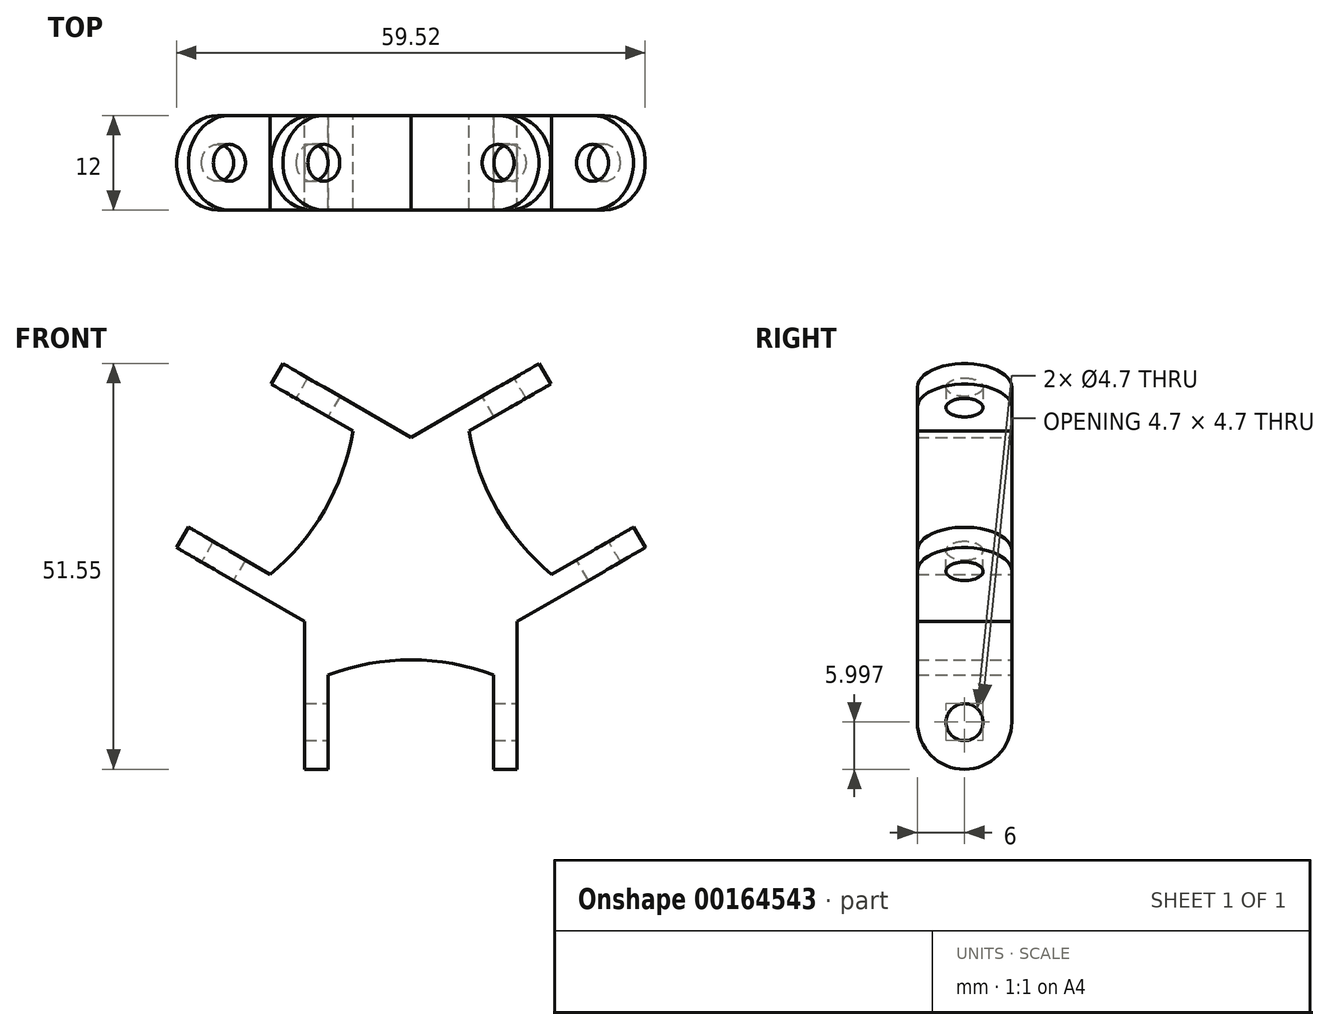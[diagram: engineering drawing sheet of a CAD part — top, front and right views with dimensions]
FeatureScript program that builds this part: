
annotation { "Feature Type Name" : "Feature", "Feature Type Description" : "" }
export const myFeature = defineFeature(function(context is Context, id is Id, definition is map)
    precondition{}
    {
        {
            var Q0;
            Q0=qCreatedBy(makeId("Front.planeOp"),FACE);
            var sketch = newSketch(context, id + "F0", { "sketchPlane" : qUnion([Q0])});
            skCircle(sketch, "E0", {"center": v(0, 0) * mm, "radius": 30 * mm, "construction": true});
            skLineSegment(sketch, "E1", {"start": v(0, 0) * mm, "end": v(0, 27.8) * mm, "construction": true});
            skLineSegment(sketch, "E2", {"start": v(0, 0) * mm, "end": v(24.85, -14.35) * mm, "construction": true});
            skLineSegment(sketch, "E3", {"start": v(38.06, 38.48) * mm, "end": v(52.36, 13.72) * mm, "construction": true});
            skLineSegment(sketch, "E4", {"start": v(0, 0) * mm, "end": v(45.2, 26.1) * mm, "construction": true});
            skLineSegment(sketch, "E5", {"start": v(17.76, 22.38) * mm, "end": v(8.6, 17.09) * mm});
            skLineSegment(sketch, "E6", {"start": v(28.26, 4.2) * mm, "end": v(19.1, -1.1) * mm});
            skArc(sketch, "E7", {"start": v(8.6, 17.09) * mm, "mid": v(12.2, 7.05) * mm, "end": v(19.1, -1.1) * mm, "construction": true});
            skLineSegment(sketch, "E8", {"start": v(19.09, 23.14) * mm, "end": v(24.34, 14.05) * mm, "construction": true});
            skLineSegment(sketch, "E9", {"start": v(24.34, 14.05) * mm, "end": v(29.59, 4.96) * mm, "construction": true});
            skLineSegment(sketch, "E10", {"start": v(13.84, 20.12) * mm, "end": v(24.34, 1.93) * mm, "construction": true});
            skLineSegment(sketch, "E11", {"start": v(13.5, -7.8) * mm, "end": v(21.63, -3.1) * mm, "construction": true});
            skLineSegment(sketch, "E12.MirrorCS", {"start": v(0, 15.59) * mm, "end": v(8.13, 20.28) * mm, "construction": true});
            skPoint(sketch, "E13.center", {"position": v(0.48, 0.8) * mm});
            skLineSegment(sketch, "E13.anchor1", {"start": v(0.48, 0.8) * mm, "end": v(0, 0) * mm, "construction": true});
            skLineSegment(sketch, "E13.anchor2", {"start": v(0.48, 0.8) * mm, "end": v(1.42, 0.8) * mm, "construction": true});
            skLineSegment(sketch, "E14", {"start": v(17.76, 22.38) * mm, "end": v(16.26, 24.98) * mm});
            skLineSegment(sketch, "E15", {"start": v(16.26, 24.98) * mm, "end": v(0, 15.59) * mm});
            skLineSegment(sketch, "E16", {"start": v(8.6, 17.09) * mm, "end": v(7.37, 16.38) * mm});
            skLineSegment(sketch, "E17", {"start": v(19.1, -1.1) * mm, "end": v(17.87, -1.8) * mm});
            skLineSegment(sketch, "E18", {"start": v(28.26, 4.2) * mm, "end": v(29.76, 1.6) * mm});
            skLineSegment(sketch, "E19", {"start": v(29.76, 1.6) * mm, "end": v(13.5, -7.8) * mm});
            skArc(sketch, "E20", {"start": v(7.37, 16.38) * mm, "mid": v(10.98, 6.34) * mm, "end": v(17.87, -1.8) * mm});
            skLineSegment(sketch, "E21.1.0", {"start": v(-29.76, 1.6) * mm, "end": v(-13.5, -7.8) * mm});
            skLineSegment(sketch, "E21.1.1", {"start": v(-28.26, 4.2) * mm, "end": v(-29.76, 1.6) * mm});
            skLineSegment(sketch, "E21.1.2", {"start": v(-28.26, 4.2) * mm, "end": v(-19.1, -1.1) * mm});
            skLineSegment(sketch, "E21.1.3", {"start": v(-19.1, -1.1) * mm, "end": v(-17.87, -1.8) * mm});
            skArc(sketch, "E21.1.4", {"start": v(-17.87, -1.8) * mm, "mid": v(-10.98, 6.34) * mm, "end": v(-7.37, 16.38) * mm});
            skLineSegment(sketch, "E21.1.5", {"start": v(-8.6, 17.09) * mm, "end": v(-7.37, 16.38) * mm});
            skLineSegment(sketch, "E21.1.6", {"start": v(-17.76, 22.38) * mm, "end": v(-8.6, 17.09) * mm});
            skLineSegment(sketch, "E21.1.7", {"start": v(-17.76, 22.38) * mm, "end": v(-16.26, 24.98) * mm});
            skLineSegment(sketch, "E21.1.8", {"start": v(-16.26, 24.98) * mm, "end": v(0, 15.59) * mm});
            skLineSegment(sketch, "E21.2.0", {"start": v(13.5, -26.57) * mm, "end": v(13.5, -7.8) * mm});
            skLineSegment(sketch, "E21.2.1", {"start": v(10.5, -26.57) * mm, "end": v(13.5, -26.57) * mm});
            skLineSegment(sketch, "E21.2.2", {"start": v(10.5, -26.57) * mm, "end": v(10.5, -16) * mm});
            skLineSegment(sketch, "E21.2.3", {"start": v(10.5, -16) * mm, "end": v(10.5, -14.57) * mm});
            skArc(sketch, "E21.2.4", {"start": v(10.5, -14.57) * mm, "mid": v(0, -12.68) * mm, "end": v(-10.5, -14.57) * mm});
            skLineSegment(sketch, "E21.2.5", {"start": v(-10.5, -16) * mm, "end": v(-10.5, -14.57) * mm});
            skLineSegment(sketch, "E21.2.6", {"start": v(-10.5, -26.57) * mm, "end": v(-10.5, -16) * mm});
            skLineSegment(sketch, "E21.2.7", {"start": v(-10.5, -26.57) * mm, "end": v(-13.5, -26.57) * mm});
            skLineSegment(sketch, "E21.2.8", {"start": v(-13.5, -26.57) * mm, "end": v(-13.5, -7.8) * mm});
            skSolve(sketch);
        }
        {
            var Q0;
            Q0=qCreatedBy(makeId("Front.planeOp"),FACE);
            var sketch = newSketch(context, id + "F1", { "sketchPlane" : qUnion([Q0])});
            skLineSegment(sketch, "E22.0", {"start": v(13.84, 20.12) * mm, "end": v(24.34, 1.93) * mm, "construction": true});
            skLineSegment(sketch, "E23.0", {"start": v(19.76, -0.14) * mm, "end": v(17.26, 4.2) * mm});
            skArc(sketch, "E23.1", {"start": v(8.7, 16.57) * mm, "mid": v(12.2, 7.05) * mm, "end": v(18.7, -0.75) * mm});
            skLineSegment(sketch, "E24.trimOffspring", {"start": v(9.76, 17.18) * mm, "end": v(8.7, 16.57) * mm});
            skLineSegment(sketch, "E25.trimOffspring", {"start": v(19.76, -0.14) * mm, "end": v(18.7, -0.75) * mm});
            skLineSegment(sketch, "E26", {"start": v(12.26, 12.85) * mm, "end": v(13.13, 13.35) * mm});
            skLineSegment(sketch, "E27", {"start": v(13.13, 13.35) * mm, "end": v(18.13, 4.7) * mm});
            skLineSegment(sketch, "E28", {"start": v(18.13, 4.7) * mm, "end": v(17.26, 4.2) * mm});
            skLineSegment(sketch, "E29.trimOffspring", {"start": v(12.26, 12.85) * mm, "end": v(9.76, 17.18) * mm});
            skPoint(sketch, "E30.orphan", {"position": v(8.6, 17.09) * mm});
            skSolve(sketch);
        }
        {
            var Q0;
            Q0 = qSketchRegion(id + "F1", true);
            var Q1;
            Q1=sQuery(id+"F1.wireOp",EDGE,"E22.0");
            revolve(context, id + "F2", {"entities" : qUnion([Q0]), "axis" : qUnion([Q1]), "revolveType" : RevolveType.FULL});
        }
        {
            var Q0;
            Q0 = qSketchRegion(id + "F0", true);
            extrude(context, id + "F3", {"entities" : qUnion([Q0]), "endBound" : BoundingType.SYMMETRIC, "depth" : 12 * mm});
        }
        {
            var Q0;
            Q0=makeQuery(id+"F3.opExtrude","SWEPT_FACE",FACE,{"disambiguationData":[OSD([sQuery(id+"F0.wireOp",EDGE,"E15")])]});
            var sketch = newSketch(context, id + "F4", { "sketchPlane" : qUnion([Q0])});
            skArc(sketch, "E31", {"start": v(20.57, -6) * mm, "mid": v(26.57, 0) * mm, "end": v(20.57, 6) * mm});
            skLineSegment(sketch, "E32", {"start": v(20.57, 6) * mm, "end": v(20.57, 9.05) * mm});
            skLineSegment(sketch, "E33", {"start": v(20.57, 9.05) * mm, "end": v(30.54, 9.05) * mm});
            skLineSegment(sketch, "E34", {"start": v(30.54, 9.05) * mm, "end": v(30.54, -9.05) * mm});
            skLineSegment(sketch, "E35", {"start": v(30.54, -9.05) * mm, "end": v(20.57, -9.05) * mm});
            skLineSegment(sketch, "E36", {"start": v(20.57, -9.05) * mm, "end": v(20.57, -6) * mm});
            skCircle(sketch, "E37", {"center": v(20.57, 0) * mm, "radius": 2.35 * mm});
            skLineSegment(sketch, "E38", {"start": v(0, 19.84) * mm, "end": v(0, -19.76) * mm, "construction": true});
            skSolve(sketch);
        }
        {
            var Q0;
            Q0 = qSketchRegion(id + "F4", true);
            extrude(context, id + "F5", {"entities" : qUnion([Q0]), "oppositeDirection" : true, "depth" : 27 * mm});
        }
        {
            var Q0;
            Q0=makeQuery(id+"F5.opExtrude","SWEPT_BODY",BODY,{"disambiguationData":[OSD([sQuery(id+"F4.wireOp",EDGE,"E31"),sQuery(id+"F4.wireOp",EDGE,"E32"),sQuery(id+"F4.wireOp",EDGE,"E33"),sQuery(id+"F4.wireOp",EDGE,"E34"),sQuery(id+"F4.wireOp",EDGE,"E35"),sQuery(id+"F4.wireOp",EDGE,"E36")])]});
            var Q1;
            Q1=makeQuery(id+"F5.opExtrude","SWEPT_BODY",BODY,{"disambiguationData":[OSD([sQuery(id+"F4.wireOp",EDGE,"E37")])]});
            var Q2;
            Q2=sQuery(id+"F0.wireOp",EDGE,"E0");
            circularPattern(context, id + "F6", {"operationType" : NewBodyOperationType.REMOVE, "entities" : qUnion([Q0, Q1]), "axis" : qUnion([Q2]), "angle" : 120 * degree, "instanceCount" : 3});
        }
        {
            var Q0;
            Q0=makeQuery(id+"F2.opRevolve","SWEPT_BODY",BODY,{"disambiguationData":[OSD([sQuery(id+"F1.wireOp",EDGE,"E23.0"),sQuery(id+"F1.wireOp",EDGE,"E23.1"),sQuery(id+"F1.wireOp",EDGE,"E24.trimOffspring"),sQuery(id+"F1.wireOp",EDGE,"E25.trimOffspring"),sQuery(id+"F1.wireOp",EDGE,"E26"),sQuery(id+"F1.wireOp",EDGE,"E27"),sQuery(id+"F1.wireOp",EDGE,"E28"),sQuery(id+"F1.wireOp",EDGE,"E29.trimOffspring")])]});
            deleteBodies(context, id + "F7", {"entities" : qUnion([Q0])});
        }
    });
